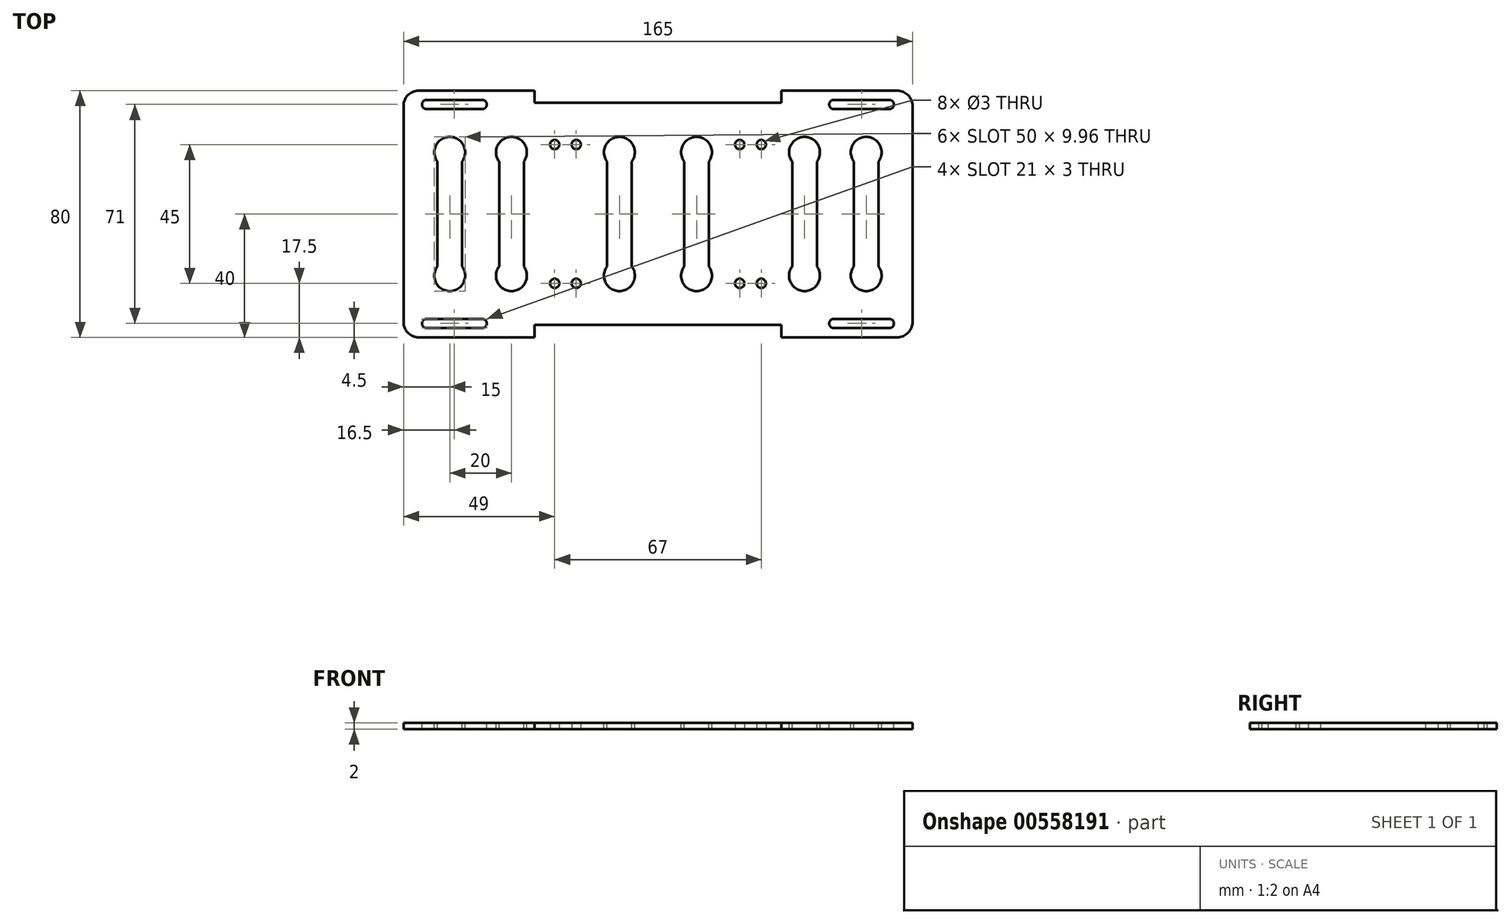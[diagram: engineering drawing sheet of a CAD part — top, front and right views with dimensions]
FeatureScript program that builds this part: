
annotation { "Feature Type Name" : "Feature", "Feature Type Description" : "" }
export const myFeature = defineFeature(function(context is Context, id is Id, definition is map)
    precondition{}
    {
        {
            var Q0;
            Q0=qCreatedBy(makeId("Top.planeOp"),FACE);
            var sketch = newSketch(context, id + "F0", { "sketchPlane" : qUnion([Q0])});
            skLineSegment(sketch, "E0.bottom", {"start": v(82.5, -40) * mm, "end": v(-82.5, -40) * mm});
            skLineSegment(sketch, "E0.top", {"start": v(82.5, 40) * mm, "end": v(-82.5, 40) * mm});
            skLineSegment(sketch, "E0.left", {"start": v(82.5, -40) * mm, "end": v(82.5, 40) * mm});
            skLineSegment(sketch, "E0.right", {"start": v(-82.5, -40) * mm, "end": v(-82.5, 40) * mm});
            skPoint(sketch, "E0.middle", {"position": v(0, 0) * mm});
            skSolve(sketch);
        }
        {
            var Q0;
            Q0=makeQuery(id+"F0.imprint","IMPRINT",FACE,{"disambiguationData":[TD([[makeQuery(id+"F0.imprint","IMPRINT",EDGE,{"derivedFrom":sQuery(id+"F0.wireOp",EDGE,"E0.bottom")}),-1.0]])]});
            extrude(context, id + "F1", {"entities" : qUnion([Q0]), "depth" : 2 * mm, "offsetDistance" : 25 * mm});
        }
        {
            var Q0;
            Q0=makeQuery(id+"F1.opExtrude","CAP_FACE",FACE,{"disambiguationData":[OSD([sQuery(id+"F0.wireOp",EDGE,"E0.bottom"),sQuery(id+"F0.wireOp",EDGE,"E0.top"),sQuery(id+"F0.wireOp",EDGE,"E0.left"),sQuery(id+"F0.wireOp",EDGE,"E0.right")])],"isStart":false});
            var sketch = newSketch(context, id + "F2", { "sketchPlane" : qUnion([Q0])});
            skLineSegment(sketch, "E1.bottom", {"start": v(-76.5, 37) * mm, "end": v(-55.5, 37) * mm});
            skLineSegment(sketch, "E1.top", {"start": v(-76.5, 34) * mm, "end": v(-55.5, 34) * mm});
            skLineSegment(sketch, "E1.left", {"start": v(-76.5, 37) * mm, "end": v(-76.5, 34) * mm});
            skLineSegment(sketch, "E1.right", {"start": v(-55.5, 37) * mm, "end": v(-55.5, 34) * mm});
            skLineSegment(sketch, "E2.bottom", {"start": v(55.5, 37) * mm, "end": v(76.5, 37) * mm});
            skLineSegment(sketch, "E2.top", {"start": v(55.5, 34) * mm, "end": v(76.5, 34) * mm});
            skLineSegment(sketch, "E2.left", {"start": v(55.5, 37) * mm, "end": v(55.5, 34) * mm});
            skLineSegment(sketch, "E2.right", {"start": v(76.5, 37) * mm, "end": v(76.5, 34) * mm});
            skLineSegment(sketch, "E3.bottom", {"start": v(55.5, -34) * mm, "end": v(76.5, -34) * mm});
            skLineSegment(sketch, "E3.top", {"start": v(55.5, -37) * mm, "end": v(76.5, -37) * mm});
            skLineSegment(sketch, "E3.left", {"start": v(55.5, -34) * mm, "end": v(55.5, -37) * mm});
            skLineSegment(sketch, "E3.right", {"start": v(76.5, -34) * mm, "end": v(76.5, -37) * mm});
            skLineSegment(sketch, "E4.bottom", {"start": v(-76.5, -34) * mm, "end": v(-55.5, -34) * mm});
            skLineSegment(sketch, "E4.top", {"start": v(-76.5, -37) * mm, "end": v(-55.5, -37) * mm});
            skLineSegment(sketch, "E4.left", {"start": v(-76.5, -34) * mm, "end": v(-76.5, -37) * mm});
            skLineSegment(sketch, "E4.right", {"start": v(-55.5, -34) * mm, "end": v(-55.5, -37) * mm});
            skSolve(sketch);
        }
        {
            var Q0;
            Q0 = qSketchRegion(id + "F2", true);
            extrude(context, id + "F3", {"entities" : qUnion([Q0]), "operationType" : NewBodyOperationType.REMOVE, "oppositeDirection" : true, "depth" : 2 * mm, "offsetDistance" : 25 * mm});
        }
        {
            var Q0;
            Q0=makeQuery(id+"F3.boolean.opBoolean","COPY",EDGE,{"derivedFrom":makeQuery(id+"F3.opExtrude","SWEPT_EDGE",EDGE,{"disambiguationData":[OSD([sQuery(id+"F2.wireOp",EDGE,"E3.top"),sQuery(id+"F2.wireOp",EDGE,"E3.right")])]})});
            var Q1;
            Q1=makeQuery(id+"F3.boolean.opBoolean","COPY",EDGE,{"derivedFrom":makeQuery(id+"F3.opExtrude","SWEPT_EDGE",EDGE,{"disambiguationData":[OSD([sQuery(id+"F2.wireOp",EDGE,"E1.top"),sQuery(id+"F2.wireOp",EDGE,"E1.right")])]})});
            var Q2;
            Q2=makeQuery(id+"F3.boolean.opBoolean","COPY",EDGE,{"derivedFrom":makeQuery(id+"F3.opExtrude","SWEPT_EDGE",EDGE,{"disambiguationData":[OSD([sQuery(id+"F2.wireOp",EDGE,"E4.top"),sQuery(id+"F2.wireOp",EDGE,"E4.right")])]})});
            var Q3;
            Q3=makeQuery(id+"F3.boolean.opBoolean","COPY",EDGE,{"derivedFrom":makeQuery(id+"F3.opExtrude","SWEPT_EDGE",EDGE,{"disambiguationData":[OSD([sQuery(id+"F2.wireOp",EDGE,"E2.top"),sQuery(id+"F2.wireOp",EDGE,"E2.right")])]})});
            var Q4;
            Q4=makeQuery(id+"F3.boolean.opBoolean","COPY",EDGE,{"derivedFrom":makeQuery(id+"F3.opExtrude","SWEPT_EDGE",EDGE,{"disambiguationData":[OSD([sQuery(id+"F2.wireOp",EDGE,"E2.bottom"),sQuery(id+"F2.wireOp",EDGE,"E2.left")])]})});
            var Q5;
            Q5=makeQuery(id+"F3.boolean.opBoolean","COPY",EDGE,{"derivedFrom":makeQuery(id+"F3.opExtrude","SWEPT_EDGE",EDGE,{"disambiguationData":[OSD([sQuery(id+"F2.wireOp",EDGE,"E3.bottom"),sQuery(id+"F2.wireOp",EDGE,"E3.left")])]})});
            var Q6;
            Q6=makeQuery(id+"F3.boolean.opBoolean","COPY",EDGE,{"derivedFrom":makeQuery(id+"F3.opExtrude","SWEPT_EDGE",EDGE,{"disambiguationData":[OSD([sQuery(id+"F2.wireOp",EDGE,"E4.bottom"),sQuery(id+"F2.wireOp",EDGE,"E4.left")])]})});
            var Q7;
            Q7=makeQuery(id+"F3.boolean.opBoolean","COPY",EDGE,{"derivedFrom":makeQuery(id+"F3.opExtrude","SWEPT_EDGE",EDGE,{"disambiguationData":[OSD([sQuery(id+"F2.wireOp",EDGE,"E1.bottom"),sQuery(id+"F2.wireOp",EDGE,"E1.left")])]})});
            var Q8;
            Q8=makeQuery(id+"F3.boolean.opBoolean","COPY",EDGE,{"derivedFrom":makeQuery(id+"F3.opExtrude","SWEPT_EDGE",EDGE,{"disambiguationData":[OSD([sQuery(id+"F2.wireOp",EDGE,"E1.top"),sQuery(id+"F2.wireOp",EDGE,"E1.left")])]})});
            var Q9;
            Q9=makeQuery(id+"F3.boolean.opBoolean","COPY",EDGE,{"derivedFrom":makeQuery(id+"F3.opExtrude","SWEPT_EDGE",EDGE,{"disambiguationData":[OSD([sQuery(id+"F2.wireOp",EDGE,"E1.bottom"),sQuery(id+"F2.wireOp",EDGE,"E1.right")])]})});
            var Q10;
            Q10=makeQuery(id+"F3.boolean.opBoolean","COPY",EDGE,{"derivedFrom":makeQuery(id+"F3.opExtrude","SWEPT_EDGE",EDGE,{"disambiguationData":[OSD([sQuery(id+"F2.wireOp",EDGE,"E2.bottom"),sQuery(id+"F2.wireOp",EDGE,"E2.right")])]})});
            var Q11;
            Q11=makeQuery(id+"F3.boolean.opBoolean","COPY",EDGE,{"derivedFrom":makeQuery(id+"F3.opExtrude","SWEPT_EDGE",EDGE,{"disambiguationData":[OSD([sQuery(id+"F2.wireOp",EDGE,"E2.top"),sQuery(id+"F2.wireOp",EDGE,"E2.left")])]})});
            var Q12;
            Q12=makeQuery(id+"F3.boolean.opBoolean","COPY",EDGE,{"derivedFrom":makeQuery(id+"F3.opExtrude","SWEPT_EDGE",EDGE,{"disambiguationData":[OSD([sQuery(id+"F2.wireOp",EDGE,"E3.bottom"),sQuery(id+"F2.wireOp",EDGE,"E3.right")])]})});
            var Q13;
            Q13=makeQuery(id+"F3.boolean.opBoolean","COPY",EDGE,{"derivedFrom":makeQuery(id+"F3.opExtrude","SWEPT_EDGE",EDGE,{"disambiguationData":[OSD([sQuery(id+"F2.wireOp",EDGE,"E3.top"),sQuery(id+"F2.wireOp",EDGE,"E3.left")])]})});
            var Q14;
            Q14=makeQuery(id+"F3.boolean.opBoolean","COPY",EDGE,{"derivedFrom":makeQuery(id+"F3.opExtrude","SWEPT_EDGE",EDGE,{"disambiguationData":[OSD([sQuery(id+"F2.wireOp",EDGE,"E4.top"),sQuery(id+"F2.wireOp",EDGE,"E4.left")])]})});
            var Q15;
            Q15=makeQuery(id+"F3.boolean.opBoolean","COPY",EDGE,{"derivedFrom":makeQuery(id+"F3.opExtrude","SWEPT_EDGE",EDGE,{"disambiguationData":[OSD([sQuery(id+"F2.wireOp",EDGE,"E4.bottom"),sQuery(id+"F2.wireOp",EDGE,"E4.right")])]})});
            fillet(context, id + "F4", {"entities" : qUnion([Q0, Q1, Q2, Q3, Q4, Q5, Q6, Q7, Q8, Q9, Q10, Q11, Q12, Q13, Q14, Q15]), "radius" : 1.5 * mm, "tangentPropagation" : true, "allowEdgeOverflow" : false});
        }
        {
            var Q0;
            Q0=makeQuery(id+"F1.opExtrude","CAP_FACE",FACE,{"disambiguationData":[OSD([sQuery(id+"F0.wireOp",EDGE,"E0.bottom"),sQuery(id+"F0.wireOp",EDGE,"E0.top"),sQuery(id+"F0.wireOp",EDGE,"E0.left"),sQuery(id+"F0.wireOp",EDGE,"E0.right")])],"isStart":false});
            var sketch = newSketch(context, id + "F5", { "sketchPlane" : qUnion([Q0])});
            skLineSegment(sketch, "E5.bottom", {"start": v(30, -22.5) * mm, "end": v(-30, -22.5) * mm, "construction": true});
            skLineSegment(sketch, "E5.top", {"start": v(30, 22.5) * mm, "end": v(-30, 22.5) * mm, "construction": true});
            skLineSegment(sketch, "E5.left", {"start": v(30, -22.5) * mm, "end": v(30, 22.5) * mm, "construction": true});
            skLineSegment(sketch, "E5.right", {"start": v(-30, -22.5) * mm, "end": v(-30, 22.5) * mm, "construction": true});
            skPoint(sketch, "E5.middle", {"position": v(0, 0) * mm});
            skLineSegment(sketch, "E6.bottom", {"start": v(33.5, -22.5) * mm, "end": v(-33.5, -22.5) * mm, "construction": true});
            skLineSegment(sketch, "E6.top", {"start": v(33.5, 22.5) * mm, "end": v(-33.5, 22.5) * mm, "construction": true});
            skLineSegment(sketch, "E6.left", {"start": v(33.5, -22.5) * mm, "end": v(33.5, 22.5) * mm, "construction": true});
            skLineSegment(sketch, "E6.right", {"start": v(-33.5, -22.5) * mm, "end": v(-33.5, 22.5) * mm, "construction": true});
            skLineSegment(sketch, "E7.bottom", {"start": v(26.5, -22.5) * mm, "end": v(-26.5, -22.5) * mm, "construction": true});
            skLineSegment(sketch, "E7.top", {"start": v(26.5, 22.5) * mm, "end": v(-26.5, 22.5) * mm, "construction": true});
            skLineSegment(sketch, "E7.left", {"start": v(26.5, -22.5) * mm, "end": v(26.5, 22.5) * mm, "construction": true});
            skLineSegment(sketch, "E7.right", {"start": v(-26.5, -22.5) * mm, "end": v(-26.5, 22.5) * mm, "construction": true});
            skCircle(sketch, "E8", {"center": v(-33.5, 22.5) * mm, "radius": 1.5 * mm});
            skCircle(sketch, "E9", {"center": v(-26.5, 22.5) * mm, "radius": 1.5 * mm});
            skCircle(sketch, "E10", {"center": v(26.5, 22.5) * mm, "radius": 1.5 * mm});
            skCircle(sketch, "E11", {"center": v(33.5, 22.5) * mm, "radius": 1.5 * mm});
            skCircle(sketch, "E12", {"center": v(33.5, -22.5) * mm, "radius": 1.5 * mm});
            skCircle(sketch, "E13", {"center": v(26.5, -22.5) * mm, "radius": 1.5 * mm});
            skCircle(sketch, "E14", {"center": v(-26.5, -22.5) * mm, "radius": 1.5 * mm});
            skCircle(sketch, "E15", {"center": v(-33.5, -22.5) * mm, "radius": 1.5 * mm});
            skSolve(sketch);
        }
        {
            var Q0;
            Q0=makeQuery(id+"F5.imprint","IMPRINT",FACE,{"disambiguationData":[TD([[makeQuery(id+"F5.imprint","IMPRINT",EDGE,{"derivedFrom":sQuery(id+"F5.wireOp",EDGE,"E8")}),-1.0]])]});
            extrude(context, id + "F6", {"entities" : qUnion([Q0]), "operationType" : NewBodyOperationType.ADD, "depth" : 2 * mm, "offsetDistance" : 25 * mm});
        }
        {
            var Q0;
            Q0=makeQuery(id+"F1.opExtrude","CAP_FACE",FACE,{"disambiguationData":[OSD([sQuery(id+"F0.wireOp",EDGE,"E0.bottom"),sQuery(id+"F0.wireOp",EDGE,"E0.top"),sQuery(id+"F0.wireOp",EDGE,"E0.left"),sQuery(id+"F0.wireOp",EDGE,"E0.right")])],"isStart":true});
            extrude(context, id + "F7", {"entities" : qUnion([Q0]), "operationType" : NewBodyOperationType.REMOVE, "oppositeDirection" : true, "depth" : 2 * mm, "offsetDistance" : 25 * mm});
        }
        {
            var Q0;
            {var subQ0=sQuery(id+"F0.wireOp",EDGE,"E0.left");var subQ1=sQuery(id+"F0.wireOp",EDGE,"E0.top");Q0=makeQuery(id+"F6.boolean.opBoolean","MERGE",EDGE,{"derivedFrom":[makeQuery(id+"F1.opExtrude","SWEPT_EDGE",EDGE,{"disambiguationData":[OSD([subQ1,subQ0])]}),makeQuery(id+"F6.opExtrude","SWEPT_EDGE",EDGE,{"disambiguationData":[OSD([subQ1,subQ0])]})]});}
            fillet(context, id + "F8", {"entities" : qUnion([Q0]), "radius" : 5 * mm, "tangentPropagation" : true, "allowEdgeOverflow" : false});
        }
        {
            var Q0;
            {var subQ0=sQuery(id+"F0.wireOp",EDGE,"E0.left");var subQ1=sQuery(id+"F0.wireOp",EDGE,"E0.bottom");Q0=makeQuery(id+"F6.boolean.opBoolean","MERGE",EDGE,{"derivedFrom":[makeQuery(id+"F1.opExtrude","SWEPT_EDGE",EDGE,{"disambiguationData":[OSD([subQ1,subQ0])]}),makeQuery(id+"F6.opExtrude","SWEPT_EDGE",EDGE,{"disambiguationData":[OSD([subQ1,subQ0])]})]});}
            var Q1;
            {var subQ0=sQuery(id+"F0.wireOp",EDGE,"E0.right");var subQ1=sQuery(id+"F0.wireOp",EDGE,"E0.bottom");Q1=makeQuery(id+"F6.boolean.opBoolean","MERGE",EDGE,{"derivedFrom":[makeQuery(id+"F1.opExtrude","SWEPT_EDGE",EDGE,{"disambiguationData":[OSD([subQ1,subQ0])]}),makeQuery(id+"F6.opExtrude","SWEPT_EDGE",EDGE,{"disambiguationData":[OSD([subQ1,subQ0])]})]});}
            var Q2;
            {var subQ0=sQuery(id+"F0.wireOp",EDGE,"E0.right");var subQ1=sQuery(id+"F0.wireOp",EDGE,"E0.top");Q2=makeQuery(id+"F6.boolean.opBoolean","MERGE",EDGE,{"derivedFrom":[makeQuery(id+"F1.opExtrude","SWEPT_EDGE",EDGE,{"disambiguationData":[OSD([subQ1,subQ0])]}),makeQuery(id+"F6.opExtrude","SWEPT_EDGE",EDGE,{"disambiguationData":[OSD([subQ1,subQ0])]})]});}
            fillet(context, id + "F9", {"entities" : qUnion([Q0, Q1, Q2]), "radius" : 5 * mm, "tangentPropagation" : true, "allowEdgeOverflow" : false});
        }
        {
            var Q0;
            Q0=makeQuery(id+"F6.opExtrude","CAP_FACE",FACE,{"disambiguationData":[OSD([sQuery(id+"F0.wireOp",EDGE,"E0.bottom"),sQuery(id+"F0.wireOp",EDGE,"E0.top"),sQuery(id+"F0.wireOp",EDGE,"E0.left"),sQuery(id+"F0.wireOp",EDGE,"E0.right"),sQuery(id+"F2.wireOp",EDGE,"E1.bottom"),sQuery(id+"F2.wireOp",EDGE,"E1.top"),sQuery(id+"F2.wireOp",EDGE,"E1.left"),sQuery(id+"F2.wireOp",EDGE,"E1.right"),sQuery(id+"F2.wireOp",EDGE,"E2.bottom"),sQuery(id+"F2.wireOp",EDGE,"E2.top"),sQuery(id+"F2.wireOp",EDGE,"E2.left"),sQuery(id+"F2.wireOp",EDGE,"E2.right"),sQuery(id+"F2.wireOp",EDGE,"E3.bottom"),sQuery(id+"F2.wireOp",EDGE,"E3.top"),sQuery(id+"F2.wireOp",EDGE,"E3.left"),sQuery(id+"F2.wireOp",EDGE,"E3.right"),sQuery(id+"F2.wireOp",EDGE,"E4.bottom"),sQuery(id+"F2.wireOp",EDGE,"E4.top"),sQuery(id+"F2.wireOp",EDGE,"E4.left"),sQuery(id+"F2.wireOp",EDGE,"E4.right"),sQuery(id+"F5.wireOp",EDGE,"E8"),sQuery(id+"F5.wireOp",EDGE,"E9"),sQuery(id+"F5.wireOp",EDGE,"E10"),sQuery(id+"F5.wireOp",EDGE,"E11"),sQuery(id+"F5.wireOp",EDGE,"E12"),sQuery(id+"F5.wireOp",EDGE,"E13"),sQuery(id+"F5.wireOp",EDGE,"E14"),sQuery(id+"F5.wireOp",EDGE,"E15")])],"isStart":false});
            var sketch = newSketch(context, id + "F10", { "sketchPlane" : qUnion([Q0])});
            skLineSegment(sketch, "E16.bottom", {"start": v(12.5, -20) * mm, "end": v(-12.5, -20) * mm, "construction": true});
            skLineSegment(sketch, "E16.top", {"start": v(12.5, 20) * mm, "end": v(-12.5, 20) * mm, "construction": true});
            skLineSegment(sketch, "E16.left", {"start": v(12.5, -20) * mm, "end": v(12.5, 20) * mm, "construction": true});
            skLineSegment(sketch, "E16.right", {"start": v(-12.5, -20) * mm, "end": v(-12.5, 20) * mm, "construction": true});
            skPoint(sketch, "E16.middle", {"position": v(0, 0) * mm});
            skLineSegment(sketch, "E17.bottom", {"start": v(-47.5, -20) * mm, "end": v(47.5, -20) * mm, "construction": true});
            skLineSegment(sketch, "E17.top", {"start": v(-47.5, 20) * mm, "end": v(47.5, 20) * mm, "construction": true});
            skLineSegment(sketch, "E17.left", {"start": v(-47.5, -20) * mm, "end": v(-47.5, 20) * mm, "construction": true});
            skLineSegment(sketch, "E17.right", {"start": v(47.5, -20) * mm, "end": v(47.5, 20) * mm, "construction": true});
            skLineSegment(sketch, "E18.bottom", {"start": v(-67.5, -20) * mm, "end": v(67.5, -20) * mm, "construction": true});
            skLineSegment(sketch, "E18.top", {"start": v(-67.5, 20) * mm, "end": v(67.5, 20) * mm, "construction": true});
            skLineSegment(sketch, "E18.left", {"start": v(-67.5, -20) * mm, "end": v(-67.5, 20) * mm, "construction": true});
            skLineSegment(sketch, "E18.right", {"start": v(67.5, -20) * mm, "end": v(67.5, 20) * mm, "construction": true});
            skCircle(sketch, "E19", {"center": v(-67.5, 20) * mm, "radius": 5 * mm});
            skCircle(sketch, "E20", {"center": v(-67.5, -20) * mm, "radius": 5 * mm});
            skCircle(sketch, "E21", {"center": v(-47.5, 20) * mm, "radius": 5 * mm});
            skCircle(sketch, "E22", {"center": v(-47.5, -20) * mm, "radius": 5 * mm});
            skCircle(sketch, "E23", {"center": v(-12.5, 20) * mm, "radius": 5 * mm});
            skCircle(sketch, "E24", {"center": v(-12.5, -20) * mm, "radius": 5 * mm});
            skCircle(sketch, "E25", {"center": v(12.5, 20) * mm, "radius": 5 * mm});
            skCircle(sketch, "E26", {"center": v(12.5, -20) * mm, "radius": 5 * mm});
            skCircle(sketch, "E27", {"center": v(47.5, 20) * mm, "radius": 5 * mm});
            skCircle(sketch, "E28", {"center": v(47.5, -20) * mm, "radius": 5 * mm});
            skCircle(sketch, "E29", {"center": v(67.5, 20) * mm, "radius": 5 * mm});
            skCircle(sketch, "E30", {"center": v(67.5, -20) * mm, "radius": 5 * mm});
            skCircle(sketch, "E31", {"center": v(-67.5, 0) * mm, "radius": 4 * mm});
            skCircle(sketch, "E32", {"center": v(-47.5, 0) * mm, "radius": 4 * mm});
            skCircle(sketch, "E33", {"center": v(-12.5, 0) * mm, "radius": 4 * mm});
            skCircle(sketch, "E34", {"center": v(12.5, 0) * mm, "radius": 4 * mm});
            skCircle(sketch, "E35", {"center": v(47.5, 0) * mm, "radius": 4 * mm});
            skCircle(sketch, "E36", {"center": v(67.5, 0) * mm, "radius": 4 * mm});
            skLineSegment(sketch, "E37.bottom", {"start": v(-71.5, 20) * mm, "end": v(-63.5, 20) * mm});
            skLineSegment(sketch, "E37.top", {"start": v(-71.5, -20) * mm, "end": v(-63.5, -20) * mm});
            skLineSegment(sketch, "E37.left", {"start": v(-71.5, 20) * mm, "end": v(-71.5, -20) * mm});
            skLineSegment(sketch, "E37.right", {"start": v(-63.5, 20) * mm, "end": v(-63.5, -20) * mm});
            skLineSegment(sketch, "E38.bottom", {"start": v(-51.5, 20) * mm, "end": v(-43.5, 20) * mm});
            skLineSegment(sketch, "E38.top", {"start": v(-51.5, -20) * mm, "end": v(-43.5, -20) * mm});
            skLineSegment(sketch, "E38.left", {"start": v(-51.5, 20) * mm, "end": v(-51.5, -20) * mm});
            skLineSegment(sketch, "E38.right", {"start": v(-43.5, 20) * mm, "end": v(-43.5, -20) * mm});
            skLineSegment(sketch, "E39.bottom", {"start": v(-16.5, 20) * mm, "end": v(-8.5, 20) * mm});
            skLineSegment(sketch, "E39.top", {"start": v(-16.5, -20) * mm, "end": v(-8.5, -20) * mm});
            skLineSegment(sketch, "E39.left", {"start": v(-16.5, 20) * mm, "end": v(-16.5, -20) * mm});
            skLineSegment(sketch, "E39.right", {"start": v(-8.5, 20) * mm, "end": v(-8.5, -20) * mm});
            skLineSegment(sketch, "E40.bottom", {"start": v(8.5, 20) * mm, "end": v(16.5, 20) * mm});
            skLineSegment(sketch, "E40.top", {"start": v(8.5, -20) * mm, "end": v(16.5, -20) * mm});
            skLineSegment(sketch, "E40.left", {"start": v(8.5, 20) * mm, "end": v(8.5, -20) * mm});
            skLineSegment(sketch, "E40.right", {"start": v(16.5, 20) * mm, "end": v(16.5, -20) * mm});
            skLineSegment(sketch, "E41.bottom", {"start": v(43.5, 20) * mm, "end": v(51.5, 20) * mm});
            skLineSegment(sketch, "E41.top", {"start": v(43.5, -20) * mm, "end": v(51.5, -20) * mm});
            skLineSegment(sketch, "E41.left", {"start": v(43.5, 20) * mm, "end": v(43.5, -20) * mm});
            skLineSegment(sketch, "E41.right", {"start": v(51.5, 20) * mm, "end": v(51.5, -20) * mm});
            skLineSegment(sketch, "E42.bottom", {"start": v(63.5, 20) * mm, "end": v(71.5, 20) * mm});
            skLineSegment(sketch, "E42.top", {"start": v(63.5, -20) * mm, "end": v(71.5, -20) * mm});
            skLineSegment(sketch, "E42.left", {"start": v(63.5, 20) * mm, "end": v(63.5, -20) * mm});
            skLineSegment(sketch, "E42.right", {"start": v(71.5, 20) * mm, "end": v(71.5, -20) * mm});
            skSolve(sketch);
        }
        {
            var Q0;
            {var subQ0=sQuery(id+"F10.wireOp",EDGE,"E37.left");var subQ1=sQuery(id+"F10.wireOp",EDGE,"E19");var subQ2=makeQuery(id+"F10.imprint","INTERSECT",VERTEX,{"derivedFrom":[subQ1,subQ0]});Q0=makeQuery(id+"F10.imprint","IMPRINT",FACE,{"disambiguationData":[TD([[makeQuery(id+"F10.imprint","IMPRINT",EDGE,{"disambiguationData":[TD([[subQ2,-1.0]])],"derivedFrom":subQ1}),-1.0]])]});}
            var Q1;
            {var subQ0=sQuery(id+"F10.wireOp",EDGE,"E37.left");var subQ1=sQuery(id+"F10.wireOp",EDGE,"E20");var subQ2=makeQuery(id+"F10.imprint","INTERSECT",VERTEX,{"derivedFrom":[subQ1,subQ0]});Q1=makeQuery(id+"F10.imprint","IMPRINT",FACE,{"disambiguationData":[TD([[makeQuery(id+"F10.imprint","IMPRINT",EDGE,{"disambiguationData":[TD([[subQ2,1.0]])],"derivedFrom":subQ1}),-1.0]])]});}
            var Q2;
            {var subQ5=sQuery(id+"F10.wireOp",EDGE,"E37.top");Q2=makeQuery(id+"F10.imprint","IMPRINT",FACE,{"disambiguationData":[TD([[makeQuery(id+"F10.imprint","IMPRINT",EDGE,{"derivedFrom":subQ5}),-1.0]])]});}
            var Q3;
            {var subQ5=sQuery(id+"F10.wireOp",EDGE,"E37.top");Q3=makeQuery(id+"F10.imprint","IMPRINT",FACE,{"disambiguationData":[TD([[makeQuery(id+"F10.imprint","IMPRINT",EDGE,{"derivedFrom":subQ5}),1.0]])]});}
            var Q4;
            {var subQ0=sQuery(id+"F10.wireOp",EDGE,"E31");var subQ1=makeQuery(id+"F10.imprint","INTERSECT",VERTEX,{"derivedFrom":[subQ0,sQuery(id+"F10.wireOp",EDGE,"E37.left")]});Q4=makeQuery(id+"F10.imprint","IMPRINT",FACE,{"disambiguationData":[TD([[makeQuery(id+"F10.imprint","IMPRINT",EDGE,{"disambiguationData":[TD([[subQ1,1.0]])],"derivedFrom":subQ0}),1.0]])]});}
            var Q5;
            {var subQ5=sQuery(id+"F10.wireOp",EDGE,"E37.bottom");Q5=makeQuery(id+"F10.imprint","IMPRINT",FACE,{"disambiguationData":[TD([[makeQuery(id+"F10.imprint","IMPRINT",EDGE,{"derivedFrom":subQ5}),-1.0]])]});}
            var Q6;
            {var subQ5=sQuery(id+"F10.wireOp",EDGE,"E37.bottom");Q6=makeQuery(id+"F10.imprint","IMPRINT",FACE,{"disambiguationData":[TD([[makeQuery(id+"F10.imprint","IMPRINT",EDGE,{"derivedFrom":subQ5}),1.0]])]});}
            var Q7;
            {var subQ5=sQuery(id+"F10.wireOp",EDGE,"E38.bottom");Q7=makeQuery(id+"F10.imprint","IMPRINT",FACE,{"disambiguationData":[TD([[makeQuery(id+"F10.imprint","IMPRINT",EDGE,{"derivedFrom":subQ5}),1.0]])]});}
            var Q8;
            {var subQ5=sQuery(id+"F10.wireOp",EDGE,"E38.bottom");Q8=makeQuery(id+"F10.imprint","IMPRINT",FACE,{"disambiguationData":[TD([[makeQuery(id+"F10.imprint","IMPRINT",EDGE,{"derivedFrom":subQ5}),-1.0]])]});}
            var Q9;
            {var subQ0=sQuery(id+"F10.wireOp",EDGE,"E38.left");var subQ1=sQuery(id+"F10.wireOp",EDGE,"E21");var subQ2=makeQuery(id+"F10.imprint","INTERSECT",VERTEX,{"derivedFrom":[subQ1,subQ0]});Q9=makeQuery(id+"F10.imprint","IMPRINT",FACE,{"disambiguationData":[TD([[makeQuery(id+"F10.imprint","IMPRINT",EDGE,{"disambiguationData":[TD([[subQ2,-1.0]])],"derivedFrom":subQ1}),-1.0]])]});}
            var Q10;
            {var subQ0=sQuery(id+"F10.wireOp",EDGE,"E32");var subQ1=makeQuery(id+"F10.imprint","INTERSECT",VERTEX,{"derivedFrom":[subQ0,sQuery(id+"F10.wireOp",EDGE,"E38.left")]});Q10=makeQuery(id+"F10.imprint","IMPRINT",FACE,{"disambiguationData":[TD([[makeQuery(id+"F10.imprint","IMPRINT",EDGE,{"disambiguationData":[TD([[subQ1,1.0]])],"derivedFrom":subQ0}),1.0]])]});}
            var Q11;
            {var subQ0=sQuery(id+"F10.wireOp",EDGE,"E38.left");var subQ1=sQuery(id+"F10.wireOp",EDGE,"E22");var subQ2=makeQuery(id+"F10.imprint","INTERSECT",VERTEX,{"derivedFrom":[subQ1,subQ0]});Q11=makeQuery(id+"F10.imprint","IMPRINT",FACE,{"disambiguationData":[TD([[makeQuery(id+"F10.imprint","IMPRINT",EDGE,{"disambiguationData":[TD([[subQ2,1.0]])],"derivedFrom":subQ1}),-1.0]])]});}
            var Q12;
            {var subQ5=sQuery(id+"F10.wireOp",EDGE,"E38.top");Q12=makeQuery(id+"F10.imprint","IMPRINT",FACE,{"disambiguationData":[TD([[makeQuery(id+"F10.imprint","IMPRINT",EDGE,{"derivedFrom":subQ5}),1.0]])]});}
            var Q13;
            {var subQ5=sQuery(id+"F10.wireOp",EDGE,"E38.top");Q13=makeQuery(id+"F10.imprint","IMPRINT",FACE,{"disambiguationData":[TD([[makeQuery(id+"F10.imprint","IMPRINT",EDGE,{"derivedFrom":subQ5}),-1.0]])]});}
            var Q14;
            {var subQ5=sQuery(id+"F10.wireOp",EDGE,"E39.bottom");Q14=makeQuery(id+"F10.imprint","IMPRINT",FACE,{"disambiguationData":[TD([[makeQuery(id+"F10.imprint","IMPRINT",EDGE,{"derivedFrom":subQ5}),1.0]])]});}
            var Q15;
            {var subQ5=sQuery(id+"F10.wireOp",EDGE,"E39.bottom");Q15=makeQuery(id+"F10.imprint","IMPRINT",FACE,{"disambiguationData":[TD([[makeQuery(id+"F10.imprint","IMPRINT",EDGE,{"derivedFrom":subQ5}),-1.0]])]});}
            var Q16;
            {var subQ0=sQuery(id+"F10.wireOp",EDGE,"E39.left");var subQ1=sQuery(id+"F10.wireOp",EDGE,"E23");var subQ2=makeQuery(id+"F10.imprint","INTERSECT",VERTEX,{"derivedFrom":[subQ1,subQ0]});Q16=makeQuery(id+"F10.imprint","IMPRINT",FACE,{"disambiguationData":[TD([[makeQuery(id+"F10.imprint","IMPRINT",EDGE,{"disambiguationData":[TD([[subQ2,-1.0]])],"derivedFrom":subQ1}),-1.0]])]});}
            var Q17;
            {var subQ0=sQuery(id+"F10.wireOp",EDGE,"E33");var subQ1=makeQuery(id+"F10.imprint","INTERSECT",VERTEX,{"derivedFrom":[subQ0,sQuery(id+"F10.wireOp",EDGE,"E39.left")]});Q17=makeQuery(id+"F10.imprint","IMPRINT",FACE,{"disambiguationData":[TD([[makeQuery(id+"F10.imprint","IMPRINT",EDGE,{"disambiguationData":[TD([[subQ1,1.0]])],"derivedFrom":subQ0}),1.0]])]});}
            var Q18;
            {var subQ0=sQuery(id+"F10.wireOp",EDGE,"E39.left");var subQ1=sQuery(id+"F10.wireOp",EDGE,"E24");var subQ2=makeQuery(id+"F10.imprint","INTERSECT",VERTEX,{"derivedFrom":[subQ1,subQ0]});Q18=makeQuery(id+"F10.imprint","IMPRINT",FACE,{"disambiguationData":[TD([[makeQuery(id+"F10.imprint","IMPRINT",EDGE,{"disambiguationData":[TD([[subQ2,1.0]])],"derivedFrom":subQ1}),-1.0]])]});}
            var Q19;
            {var subQ5=sQuery(id+"F10.wireOp",EDGE,"E39.top");Q19=makeQuery(id+"F10.imprint","IMPRINT",FACE,{"disambiguationData":[TD([[makeQuery(id+"F10.imprint","IMPRINT",EDGE,{"derivedFrom":subQ5}),1.0]])]});}
            var Q20;
            {var subQ5=sQuery(id+"F10.wireOp",EDGE,"E39.top");Q20=makeQuery(id+"F10.imprint","IMPRINT",FACE,{"disambiguationData":[TD([[makeQuery(id+"F10.imprint","IMPRINT",EDGE,{"derivedFrom":subQ5}),-1.0]])]});}
            var Q21;
            {var subQ5=sQuery(id+"F10.wireOp",EDGE,"E40.bottom");Q21=makeQuery(id+"F10.imprint","IMPRINT",FACE,{"disambiguationData":[TD([[makeQuery(id+"F10.imprint","IMPRINT",EDGE,{"derivedFrom":subQ5}),1.0]])]});}
            var Q22;
            {var subQ5=sQuery(id+"F10.wireOp",EDGE,"E40.bottom");Q22=makeQuery(id+"F10.imprint","IMPRINT",FACE,{"disambiguationData":[TD([[makeQuery(id+"F10.imprint","IMPRINT",EDGE,{"derivedFrom":subQ5}),-1.0]])]});}
            var Q23;
            {var subQ0=sQuery(id+"F10.wireOp",EDGE,"E40.left");var subQ1=sQuery(id+"F10.wireOp",EDGE,"E25");var subQ2=makeQuery(id+"F10.imprint","INTERSECT",VERTEX,{"derivedFrom":[subQ1,subQ0]});Q23=makeQuery(id+"F10.imprint","IMPRINT",FACE,{"disambiguationData":[TD([[makeQuery(id+"F10.imprint","IMPRINT",EDGE,{"disambiguationData":[TD([[subQ2,-1.0]])],"derivedFrom":subQ1}),-1.0]])]});}
            var Q24;
            {var subQ0=sQuery(id+"F10.wireOp",EDGE,"E34");var subQ1=makeQuery(id+"F10.imprint","INTERSECT",VERTEX,{"derivedFrom":[subQ0,sQuery(id+"F10.wireOp",EDGE,"E40.left")]});Q24=makeQuery(id+"F10.imprint","IMPRINT",FACE,{"disambiguationData":[TD([[makeQuery(id+"F10.imprint","IMPRINT",EDGE,{"disambiguationData":[TD([[subQ1,1.0]])],"derivedFrom":subQ0}),1.0]])]});}
            var Q25;
            {var subQ0=sQuery(id+"F10.wireOp",EDGE,"E40.left");var subQ1=sQuery(id+"F10.wireOp",EDGE,"E26");var subQ2=makeQuery(id+"F10.imprint","INTERSECT",VERTEX,{"derivedFrom":[subQ1,subQ0]});Q25=makeQuery(id+"F10.imprint","IMPRINT",FACE,{"disambiguationData":[TD([[makeQuery(id+"F10.imprint","IMPRINT",EDGE,{"disambiguationData":[TD([[subQ2,1.0]])],"derivedFrom":subQ1}),-1.0]])]});}
            var Q26;
            {var subQ5=sQuery(id+"F10.wireOp",EDGE,"E40.top");Q26=makeQuery(id+"F10.imprint","IMPRINT",FACE,{"disambiguationData":[TD([[makeQuery(id+"F10.imprint","IMPRINT",EDGE,{"derivedFrom":subQ5}),1.0]])]});}
            var Q27;
            {var subQ5=sQuery(id+"F10.wireOp",EDGE,"E40.top");Q27=makeQuery(id+"F10.imprint","IMPRINT",FACE,{"disambiguationData":[TD([[makeQuery(id+"F10.imprint","IMPRINT",EDGE,{"derivedFrom":subQ5}),-1.0]])]});}
            var Q28;
            {var subQ5=sQuery(id+"F10.wireOp",EDGE,"E41.bottom");Q28=makeQuery(id+"F10.imprint","IMPRINT",FACE,{"disambiguationData":[TD([[makeQuery(id+"F10.imprint","IMPRINT",EDGE,{"derivedFrom":subQ5}),1.0]])]});}
            var Q29;
            {var subQ5=sQuery(id+"F10.wireOp",EDGE,"E41.bottom");Q29=makeQuery(id+"F10.imprint","IMPRINT",FACE,{"disambiguationData":[TD([[makeQuery(id+"F10.imprint","IMPRINT",EDGE,{"derivedFrom":subQ5}),-1.0]])]});}
            var Q30;
            {var subQ0=sQuery(id+"F10.wireOp",EDGE,"E41.left");var subQ1=sQuery(id+"F10.wireOp",EDGE,"E27");var subQ2=makeQuery(id+"F10.imprint","INTERSECT",VERTEX,{"derivedFrom":[subQ1,subQ0]});Q30=makeQuery(id+"F10.imprint","IMPRINT",FACE,{"disambiguationData":[TD([[makeQuery(id+"F10.imprint","IMPRINT",EDGE,{"disambiguationData":[TD([[subQ2,-1.0]])],"derivedFrom":subQ1}),-1.0]])]});}
            var Q31;
            {var subQ0=sQuery(id+"F10.wireOp",EDGE,"E35");var subQ1=makeQuery(id+"F10.imprint","INTERSECT",VERTEX,{"derivedFrom":[subQ0,sQuery(id+"F10.wireOp",EDGE,"E41.left")]});Q31=makeQuery(id+"F10.imprint","IMPRINT",FACE,{"disambiguationData":[TD([[makeQuery(id+"F10.imprint","IMPRINT",EDGE,{"disambiguationData":[TD([[subQ1,1.0]])],"derivedFrom":subQ0}),1.0]])]});}
            var Q32;
            {var subQ0=sQuery(id+"F10.wireOp",EDGE,"E41.left");var subQ1=sQuery(id+"F10.wireOp",EDGE,"E28");var subQ2=makeQuery(id+"F10.imprint","INTERSECT",VERTEX,{"derivedFrom":[subQ1,subQ0]});Q32=makeQuery(id+"F10.imprint","IMPRINT",FACE,{"disambiguationData":[TD([[makeQuery(id+"F10.imprint","IMPRINT",EDGE,{"disambiguationData":[TD([[subQ2,1.0]])],"derivedFrom":subQ1}),-1.0]])]});}
            var Q33;
            {var subQ5=sQuery(id+"F10.wireOp",EDGE,"E41.top");Q33=makeQuery(id+"F10.imprint","IMPRINT",FACE,{"disambiguationData":[TD([[makeQuery(id+"F10.imprint","IMPRINT",EDGE,{"derivedFrom":subQ5}),1.0]])]});}
            var Q34;
            {var subQ5=sQuery(id+"F10.wireOp",EDGE,"E41.top");Q34=makeQuery(id+"F10.imprint","IMPRINT",FACE,{"disambiguationData":[TD([[makeQuery(id+"F10.imprint","IMPRINT",EDGE,{"derivedFrom":subQ5}),-1.0]])]});}
            var Q35;
            {var subQ5=sQuery(id+"F10.wireOp",EDGE,"E42.bottom");Q35=makeQuery(id+"F10.imprint","IMPRINT",FACE,{"disambiguationData":[TD([[makeQuery(id+"F10.imprint","IMPRINT",EDGE,{"derivedFrom":subQ5}),1.0]])]});}
            var Q36;
            {var subQ5=sQuery(id+"F10.wireOp",EDGE,"E42.bottom");Q36=makeQuery(id+"F10.imprint","IMPRINT",FACE,{"disambiguationData":[TD([[makeQuery(id+"F10.imprint","IMPRINT",EDGE,{"derivedFrom":subQ5}),-1.0]])]});}
            var Q37;
            {var subQ0=sQuery(id+"F10.wireOp",EDGE,"E42.left");var subQ1=sQuery(id+"F10.wireOp",EDGE,"E29");var subQ2=makeQuery(id+"F10.imprint","INTERSECT",VERTEX,{"derivedFrom":[subQ1,subQ0]});Q37=makeQuery(id+"F10.imprint","IMPRINT",FACE,{"disambiguationData":[TD([[makeQuery(id+"F10.imprint","IMPRINT",EDGE,{"disambiguationData":[TD([[subQ2,-1.0]])],"derivedFrom":subQ1}),-1.0]])]});}
            var Q38;
            {var subQ0=sQuery(id+"F10.wireOp",EDGE,"E36");var subQ1=makeQuery(id+"F10.imprint","INTERSECT",VERTEX,{"derivedFrom":[subQ0,sQuery(id+"F10.wireOp",EDGE,"E42.left")]});Q38=makeQuery(id+"F10.imprint","IMPRINT",FACE,{"disambiguationData":[TD([[makeQuery(id+"F10.imprint","IMPRINT",EDGE,{"disambiguationData":[TD([[subQ1,1.0]])],"derivedFrom":subQ0}),1.0]])]});}
            var Q39;
            {var subQ0=sQuery(id+"F10.wireOp",EDGE,"E42.left");var subQ1=sQuery(id+"F10.wireOp",EDGE,"E30");var subQ2=makeQuery(id+"F10.imprint","INTERSECT",VERTEX,{"derivedFrom":[subQ1,subQ0]});Q39=makeQuery(id+"F10.imprint","IMPRINT",FACE,{"disambiguationData":[TD([[makeQuery(id+"F10.imprint","IMPRINT",EDGE,{"disambiguationData":[TD([[subQ2,1.0]])],"derivedFrom":subQ1}),-1.0]])]});}
            var Q40;
            {var subQ5=sQuery(id+"F10.wireOp",EDGE,"E42.top");Q40=makeQuery(id+"F10.imprint","IMPRINT",FACE,{"disambiguationData":[TD([[makeQuery(id+"F10.imprint","IMPRINT",EDGE,{"derivedFrom":subQ5}),1.0]])]});}
            var Q41;
            {var subQ5=sQuery(id+"F10.wireOp",EDGE,"E42.top");Q41=makeQuery(id+"F10.imprint","IMPRINT",FACE,{"disambiguationData":[TD([[makeQuery(id+"F10.imprint","IMPRINT",EDGE,{"derivedFrom":subQ5}),-1.0]])]});}
            extrude(context, id + "F11", {"entities" : qUnion([Q0, Q1, Q2, Q3, Q4, Q5, Q6, Q7, Q8, Q9, Q10, Q11, Q12, Q13, Q14, Q15, Q16, Q17, Q18, Q19, Q20, Q21, Q22, Q23, Q24, Q25, Q26, Q27, Q28, Q29, Q30, Q31, Q32, Q33, Q34, Q35, Q36, Q37, Q38, Q39, Q40, Q41]), "operationType" : NewBodyOperationType.REMOVE, "endBound" : BoundingType.THROUGH_ALL, "oppositeDirection" : true, "depth" : 25 * mm, "offsetDistance" : 25 * mm});
        }
        {
            var Q0;
            Q0=makeQuery(id+"F6.opExtrude","CAP_FACE",FACE,{"disambiguationData":[OSD([sQuery(id+"F0.wireOp",EDGE,"E0.bottom"),sQuery(id+"F0.wireOp",EDGE,"E0.top"),sQuery(id+"F0.wireOp",EDGE,"E0.left"),sQuery(id+"F0.wireOp",EDGE,"E0.right"),sQuery(id+"F2.wireOp",EDGE,"E1.bottom"),sQuery(id+"F2.wireOp",EDGE,"E1.top"),sQuery(id+"F2.wireOp",EDGE,"E1.left"),sQuery(id+"F2.wireOp",EDGE,"E1.right"),sQuery(id+"F2.wireOp",EDGE,"E2.bottom"),sQuery(id+"F2.wireOp",EDGE,"E2.top"),sQuery(id+"F2.wireOp",EDGE,"E2.left"),sQuery(id+"F2.wireOp",EDGE,"E2.right"),sQuery(id+"F2.wireOp",EDGE,"E3.bottom"),sQuery(id+"F2.wireOp",EDGE,"E3.top"),sQuery(id+"F2.wireOp",EDGE,"E3.left"),sQuery(id+"F2.wireOp",EDGE,"E3.right"),sQuery(id+"F2.wireOp",EDGE,"E4.bottom"),sQuery(id+"F2.wireOp",EDGE,"E4.top"),sQuery(id+"F2.wireOp",EDGE,"E4.left"),sQuery(id+"F2.wireOp",EDGE,"E4.right"),sQuery(id+"F5.wireOp",EDGE,"E8"),sQuery(id+"F5.wireOp",EDGE,"E9"),sQuery(id+"F5.wireOp",EDGE,"E10"),sQuery(id+"F5.wireOp",EDGE,"E11"),sQuery(id+"F5.wireOp",EDGE,"E12"),sQuery(id+"F5.wireOp",EDGE,"E13"),sQuery(id+"F5.wireOp",EDGE,"E14"),sQuery(id+"F5.wireOp",EDGE,"E15")])],"isStart":false});
            var sketch = newSketch(context, id + "F12", { "sketchPlane" : qUnion([Q0])});
            skLineSegment(sketch, "E43.bottom", {"start": v(40, -36) * mm, "end": v(-40, -36) * mm});
            skLineSegment(sketch, "E43.top", {"start": v(40, -44) * mm, "end": v(-40, -44) * mm});
            skLineSegment(sketch, "E43.left", {"start": v(40, -36) * mm, "end": v(40, -44) * mm});
            skLineSegment(sketch, "E43.right", {"start": v(-40, -36) * mm, "end": v(-40, -44) * mm});
            skPoint(sketch, "E43.middle", {"position": v(0, -40) * mm});
            skLineSegment(sketch, "E44.bottom", {"start": v(-40, 36) * mm, "end": v(40, 36) * mm});
            skLineSegment(sketch, "E44.top", {"start": v(-40, 44) * mm, "end": v(40, 44) * mm});
            skLineSegment(sketch, "E44.left", {"start": v(-40, 36) * mm, "end": v(-40, 44) * mm});
            skLineSegment(sketch, "E44.right", {"start": v(40, 36) * mm, "end": v(40, 44) * mm});
            skPoint(sketch, "E44.middle", {"position": v(0, 40) * mm});
            skSolve(sketch);
        }
        {
            var Q0;
            Q0 = qSketchRegion(id + "F12", true);
            extrude(context, id + "F13", {"entities" : qUnion([Q0]), "operationType" : NewBodyOperationType.REMOVE, "endBound" : BoundingType.THROUGH_ALL, "oppositeDirection" : true, "depth" : 25 * mm, "offsetDistance" : 25 * mm});
        }
    });
